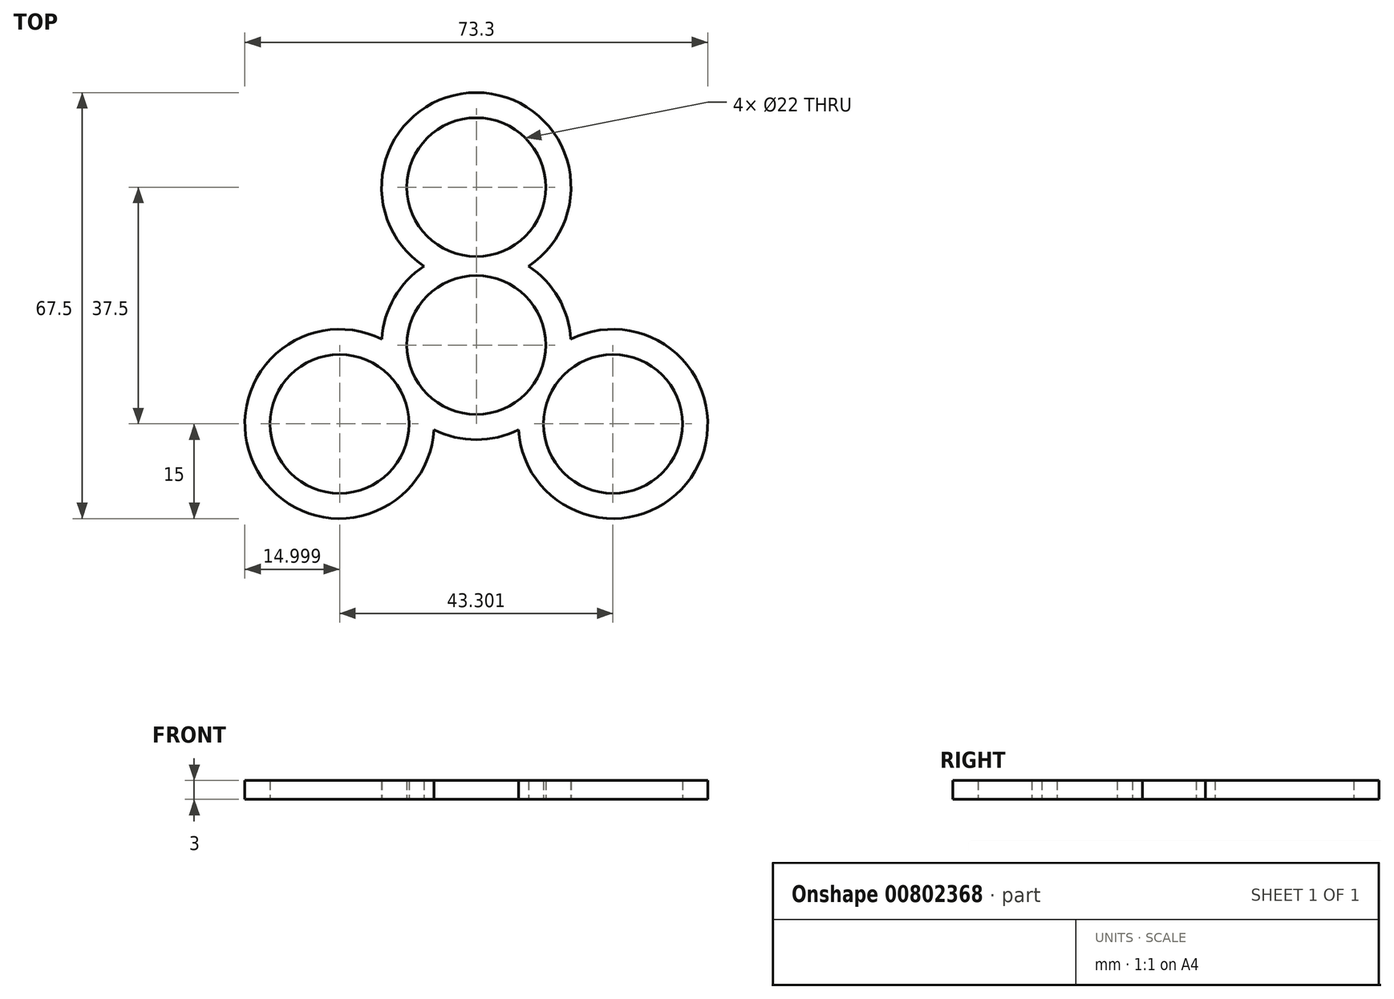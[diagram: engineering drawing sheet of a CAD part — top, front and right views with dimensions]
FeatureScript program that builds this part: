
annotation { "Feature Type Name" : "Feature", "Feature Type Description" : "" }
export const myFeature = defineFeature(function(context is Context, id is Id, definition is map)
    precondition{}
    {
        {
            var Q0;
            Q0=qCreatedBy(makeId("Top.planeOp"),FACE);
            var sketch = newSketch(context, id + "F0", { "sketchPlane" : qUnion([Q0])});
            skArc(sketch, "E0", {"start": v(9.53, 5.5) * mm, "mid": v(0, 11) * mm, "end": v(-9.53, 5.5) * mm});
            skCircle(sketch, "E1", {"center": v(0, 25) * mm, "radius": 11 * mm});
            skArc(sketch, "E2", {"start": v(-8.3, 12.5) * mm, "mid": v(-10.93, 10.27) * mm, "end": v(-13, 7.5) * mm});
            skArc(sketch, "E3.trimOffspring", {"start": v(8.3, 12.5) * mm, "mid": v(0, 40) * mm, "end": v(-8.3, 12.5) * mm});
            skArc(sketch, "E4.trimOffspring", {"start": v(13, 7.5) * mm, "mid": v(10.93, 10.27) * mm, "end": v(8.3, 12.5) * mm});
            skArc(sketch, "E5.1.0", {"start": v(-14.97, 0.93) * mm, "mid": v(-34.64, -20) * mm, "end": v(-6.68, -13.43) * mm});
            skCircle(sketch, "E5.1.1", {"center": v(-21.65, -12.5) * mm, "radius": 11 * mm});
            skArc(sketch, "E5.1.2", {"start": v(-13, 7.5) * mm, "mid": v(-14.36, 4.33) * mm, "end": v(-14.97, 0.93) * mm});
            skArc(sketch, "E5.1.3", {"start": v(-6.68, -13.43) * mm, "mid": v(-3.43, -14.6) * mm, "end": v(0, -15) * mm});
            skArc(sketch, "E5.1.4", {"start": v(-9.53, 5.5) * mm, "mid": v(-9.53, -5.5) * mm, "end": v(0, -11) * mm});
            skArc(sketch, "E5.2.0", {"start": v(6.68, -13.43) * mm, "mid": v(34.64, -20) * mm, "end": v(14.97, 0.93) * mm});
            skCircle(sketch, "E5.2.1", {"center": v(21.65, -12.5) * mm, "radius": 11 * mm});
            skArc(sketch, "E5.2.2", {"start": v(0, -15) * mm, "mid": v(3.43, -14.6) * mm, "end": v(6.68, -13.43) * mm});
            skArc(sketch, "E5.2.3", {"start": v(14.97, 0.93) * mm, "mid": v(14.36, 4.33) * mm, "end": v(13, 7.5) * mm});
            skArc(sketch, "E5.2.4", {"start": v(0, -11) * mm, "mid": v(9.53, -5.5) * mm, "end": v(9.53, 5.5) * mm});
            skSolve(sketch);
        }
        {
            var Q0;
            Q0 = qSketchRegion(id + "F0", true);
            extrude(context, id + "F1", {"entities" : qUnion([Q0]), "depth" : 3 * mm, "offsetDistance" : 25 * mm});
        }
    });
